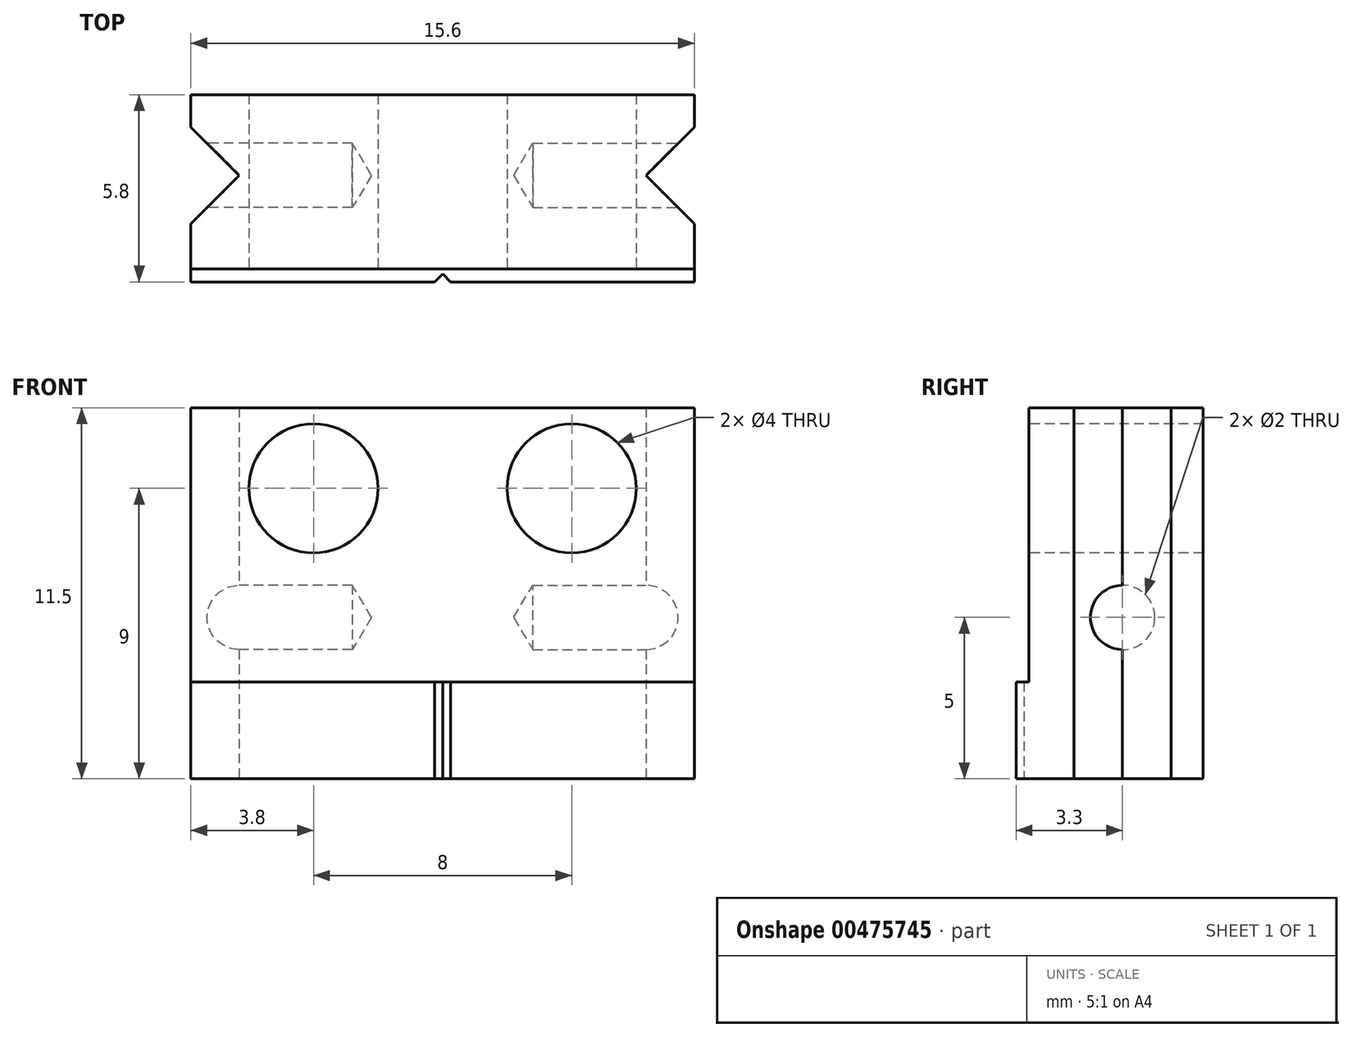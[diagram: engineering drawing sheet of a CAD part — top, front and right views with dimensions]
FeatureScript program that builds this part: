
annotation { "Feature Type Name" : "Feature", "Feature Type Description" : "" }
export const myFeature = defineFeature(function(context is Context, id is Id, definition is map)
    precondition{}
    {
        {
            var Q0;
            Q0=qCreatedBy(makeId("Front.planeOp"),FACE);
            var sketch = newSketch(context, id + "F0", { "sketchPlane" : qUnion([Q0])});
            skLineSegment(sketch, "E0.bottom", {"start": v(-7.8, 4.6) * mm, "end": v(7.8, 4.6) * mm});
            skLineSegment(sketch, "E0.top", {"start": v(-7.8, -6.9) * mm, "end": v(7.8, -6.9) * mm});
            skLineSegment(sketch, "E0.left", {"start": v(-7.8, 4.6) * mm, "end": v(-7.8, -6.9) * mm});
            skLineSegment(sketch, "E0.right", {"start": v(7.8, 4.6) * mm, "end": v(7.8, -6.9) * mm});
            skPoint(sketch, "E1", {"position": v(0, 4.6) * mm});
            skSolve(sketch);
        }
        {
            var Q0;
            Q0=makeQuery(id+"F0.imprint","IMPRINT",FACE,{"disambiguationData":[TD([[makeQuery(id+"F0.imprint","IMPRINT",EDGE,{"derivedFrom":sQuery(id+"F0.wireOp",EDGE,"E0.bottom")}),-1.0]])]});
            extrude(context, id + "F1", {"entities" : qUnion([Q0]), "oppositeDirection" : true, "depth" : 5.4 * mm});
        }
        {
            var Q0;
            Q0=makeQuery(id+"F1.opExtrude","CAP_FACE",FACE,{"disambiguationData":[OSD([sQuery(id+"F0.wireOp",EDGE,"E0.bottom"),sQuery(id+"F0.wireOp",EDGE,"E0.top"),sQuery(id+"F0.wireOp",EDGE,"E0.left"),sQuery(id+"F0.wireOp",EDGE,"E0.right")])],"isStart":true});
            var sketch = newSketch(context, id + "F2", { "sketchPlane" : qUnion([Q0])});
            skLineSegment(sketch, "E2.bottom", {"start": v(-7.8, -6.9) * mm, "end": v(7.8, -6.9) * mm});
            skLineSegment(sketch, "E2.top", {"start": v(-7.8, -3.9) * mm, "end": v(7.8, -3.9) * mm});
            skLineSegment(sketch, "E2.left", {"start": v(-7.8, -6.9) * mm, "end": v(-7.8, -3.9) * mm});
            skLineSegment(sketch, "E2.right", {"start": v(7.8, -6.9) * mm, "end": v(7.8, -3.9) * mm});
            skSolve(sketch);
        }
        {
            var Q0;
            Q0=qSketchRegion(id+"F2",true);
            var Q1;
            Q1=makeQuery(id+"F2.imprint","IMPRINT",FACE,{"disambiguationData":[TD([[makeQuery(id+"F2.imprint","IMPRINT",EDGE,{"derivedFrom":sQuery(id+"F2.wireOp",EDGE,"E2.bottom")}),1.0]])]});
            extrude(context, id + "F3", {"entities" : qUnion([Q0, Q1]), "operationType" : NewBodyOperationType.ADD, "depth" : 0.4 * mm});
        }
        {
            var Q0;
            {var subQ0=sQuery(id+"FxwlEzSzm6KvwoR_0.wireOp",EDGE,"2HalEMAT-7wpH-UPtH-xPY5-z2PY34kLNntl.right");Q0=makeQuery(id+"F3.boolean.opBoolean","MERGE",FACE,{"derivedFrom":[makeQuery(id+"F1.boolean.opBoolean","MERGE",FACE,{"derivedFrom":[makeQuery(id+"FRxiTronEwWI8pY_0.opExtrude","SWEPT_FACE",FACE,{"disambiguationData":[OSD([subQ0]),TDD([makeQuery(id+"FxwlEzSzm6KvwoR_0.imprint","IMPRINT",EDGE,{"disambiguationData":[TD([[makeQuery(id+"FxwlEzSzm6KvwoR_0.imprint","INTERSECT",VERTEX,{"derivedFrom":[sQuery(id+"FxwlEzSzm6KvwoR_0.wireOp",EDGE,"2HalEMAT-7wpH-UPtH-xPY5-z2PY34kLNntl.bottom"),subQ0]}),-1.0]])],"derivedFrom":subQ0})])]}),makeQuery(id+"F1.opExtrude","SWEPT_FACE",FACE,{"disambiguationData":[OSD([sQuery(id+"F0.wireOp",EDGE,"E0.right")])]})]}),makeQuery(id+"F3.opExtrude","SWEPT_FACE",FACE,{"disambiguationData":[OSD([sQuery(id+"F2.wireOp",EDGE,"E2.right")])]})]});}
            var sketch = newSketch(context, id + "F4", { "sketchPlane" : qUnion([Q0])});
            skPoint(sketch, "E3", {"position": v(2.9, -1.9) * mm});
            skSolve(sketch);
        }
        {
            var Q0;
            {var subQ0=sQuery(id+"FxwlEzSzm6KvwoR_0.wireOp",EDGE,"2HalEMAT-7wpH-UPtH-xPY5-z2PY34kLNntl.left");Q0=makeQuery(id+"F3.boolean.opBoolean","MERGE",FACE,{"derivedFrom":[makeQuery(id+"F1.boolean.opBoolean","MERGE",FACE,{"derivedFrom":[makeQuery(id+"FRxiTronEwWI8pY_0.opExtrude","SWEPT_FACE",FACE,{"disambiguationData":[OSD([subQ0]),TDD([makeQuery(id+"FxwlEzSzm6KvwoR_0.imprint","IMPRINT",EDGE,{"disambiguationData":[TD([[makeQuery(id+"FxwlEzSzm6KvwoR_0.imprint","INTERSECT",VERTEX,{"derivedFrom":[sQuery(id+"FxwlEzSzm6KvwoR_0.wireOp",EDGE,"2HalEMAT-7wpH-UPtH-xPY5-z2PY34kLNntl.bottom"),subQ0]}),-1.0]])],"derivedFrom":subQ0})])]}),makeQuery(id+"F1.opExtrude","SWEPT_FACE",FACE,{"disambiguationData":[OSD([sQuery(id+"F0.wireOp",EDGE,"E0.left")])]})]}),makeQuery(id+"F3.opExtrude","SWEPT_FACE",FACE,{"disambiguationData":[OSD([sQuery(id+"F2.wireOp",EDGE,"E2.left")])]})]});}
            var sketch = newSketch(context, id + "F5", { "sketchPlane" : qUnion([Q0])});
            skPoint(sketch, "E4", {"position": v(-2.9, -1.9) * mm});
            skSolve(sketch);
        }
        {
            var Q0;
            Q0=sQuery(id+"F4.wireOp",VERTEX,"E3");
            var Q1;
            Q1=sQuery(id+"F5.wireOp",VERTEX,"E4");
            var Q2;
            Q2=makeQuery(id+"F1.opExtrude","SWEPT_BODY",BODY,{"disambiguationData":[OSD([sQuery(id+"F0.wireOp",EDGE,"E0.bottom"),sQuery(id+"F0.wireOp",EDGE,"E0.top"),sQuery(id+"F0.wireOp",EDGE,"E0.left"),sQuery(id+"F0.wireOp",EDGE,"E0.right")])]});
            hole(context, id + "F6", {"style" : HoleStyle.SIMPLE, "endStyle" : HoleEndStyle.BLIND, "holeDiameter" : 2 * mm, "holeDepth" : 5 * mm, "tappedDepth" : 12 * mm, "tapClearance" : 3, "locations" : qUnion([Q0, Q1]), "scope" : qUnion([Q2])});
        }
        {
            var Q0;
            Q0=makeQuery(id+"F1.opExtrude","SWEPT_FACE",FACE,{"disambiguationData":[OSD([sQuery(id+"F0.wireOp",EDGE,"E0.top")])]});
            var sketch = newSketch(context, id + "F7", { "sketchPlane" : qUnion([Q0])});
            skLineSegment(sketch, "E5", {"start": v(7.8, -1.4) * mm, "end": v(6.3, -2.9) * mm});
            skLineSegment(sketch, "E6", {"start": v(6.3, -2.9) * mm, "end": v(7.8, -4.4) * mm});
            skLineSegment(sketch, "E7", {"start": v(7.8, -2.9) * mm, "end": v(-7.8, -2.9) * mm, "construction": true});
            skLineSegment(sketch, "E8.MirrorCS", {"start": v(-7.8, -1.4) * mm, "end": v(-6.3, -2.9) * mm});
            skLineSegment(sketch, "E9.MirrorCS", {"start": v(-6.3, -2.9) * mm, "end": v(-7.8, -4.4) * mm});
            skSolve(sketch);
        }
        {
            var Q0;
            {var subQ0=sQuery(id+"F7.wireOp",EDGE,"E8.MirrorCS");Q0=makeQuery(id+"F7.imprint","IMPRINT",FACE,{"disambiguationData":[TD([[makeQuery(id+"F7.imprint","IMPRINT",EDGE,{"derivedFrom":subQ0}),-1.0]])]});}
            var Q1;
            {var subQ0=sQuery(id+"F7.wireOp",EDGE,"E5");Q1=makeQuery(id+"F7.imprint","IMPRINT",FACE,{"disambiguationData":[TD([[makeQuery(id+"F7.imprint","IMPRINT",EDGE,{"derivedFrom":subQ0}),1.0]])]});}
            extrude(context, id + "F8", {"entities" : qUnion([Q0, Q1]), "operationType" : NewBodyOperationType.REMOVE, "oppositeDirection" : true, "depth" : 25 * mm});
        }
        {
            var Q0;
            Q0=makeQuery(id+"F3.boolean.opBoolean","MERGE",FACE,{"derivedFrom":[makeQuery(id+"F1.opExtrude","SWEPT_FACE",FACE,{"disambiguationData":[OSD([sQuery(id+"F0.wireOp",EDGE,"E0.top")])]}),makeQuery(id+"F3.opExtrude","SWEPT_FACE",FACE,{"disambiguationData":[OSD([sQuery(id+"F2.wireOp",EDGE,"E2.bottom")])]})]});
            var sketch = newSketch(context, id + "F9", { "sketchPlane" : qUnion([Q0])});
            skLineSegment(sketch, "E10", {"start": v(0, 0.4) * mm, "end": v(0, -5.4) * mm, "construction": true});
            skLineSegment(sketch, "E11", {"start": v(0, 0.15) * mm, "end": v(0.25, 0.4) * mm});
            skLineSegment(sketch, "E12", {"start": v(0, 0.15) * mm, "end": v(-0.25, 0.4) * mm});
            skSolve(sketch);
        }
        {
            var Q0;
            {var subQ0=sQuery(id+"F9.wireOp",EDGE,"E11");Q0=makeQuery(id+"F9.imprint","IMPRINT",FACE,{"disambiguationData":[TD([[makeQuery(id+"F9.imprint","IMPRINT",EDGE,{"derivedFrom":subQ0}),1.0]])]});}
            extrude(context, id + "F10", {"entities" : qUnion([Q0]), "operationType" : NewBodyOperationType.REMOVE, "endBound" : BoundingType.UP_TO_NEXT, "oppositeDirection" : true, "depth" : 25 * mm});
        }
        {
            var Q0;
            Q0=makeQuery(id+"F1.opExtrude","CAP_FACE",FACE,{"disambiguationData":[OSD([sQuery(id+"F0.wireOp",EDGE,"E0.bottom"),sQuery(id+"F0.wireOp",EDGE,"E0.top"),sQuery(id+"F0.wireOp",EDGE,"E0.left"),sQuery(id+"F0.wireOp",EDGE,"E0.right")])],"isStart":true});
            var sketch = newSketch(context, id + "F11", { "sketchPlane" : qUnion([Q0])});
            skPoint(sketch, "E13", {"position": v(-4, 2.1) * mm});
            skPoint(sketch, "E14.MirrorP", {"position": v(4, 2.1) * mm});
            skSolve(sketch);
        }
        {
            var Q0;
            Q0=sQuery(id+"F11.wireOp",VERTEX,"E13");
            var Q1;
            Q1=sQuery(id+"F11.wireOp",VERTEX,"E14.MirrorP");
            var Q2;
            Q2=makeQuery(id+"F1.opExtrude","SWEPT_BODY",BODY,{"disambiguationData":[OSD([sQuery(id+"F0.wireOp",EDGE,"E0.bottom"),sQuery(id+"F0.wireOp",EDGE,"E0.top"),sQuery(id+"F0.wireOp",EDGE,"E0.left"),sQuery(id+"F0.wireOp",EDGE,"E0.right")])]});
            hole(context, id + "F12", {"style" : HoleStyle.SIMPLE, "endStyle" : HoleEndStyle.THROUGH, "holeDiameter" : 4 * mm, "tappedDepth" : 12 * mm, "tapClearance" : 3, "locations" : qUnion([Q0, Q1]), "scope" : qUnion([Q2])});
        }
    });
